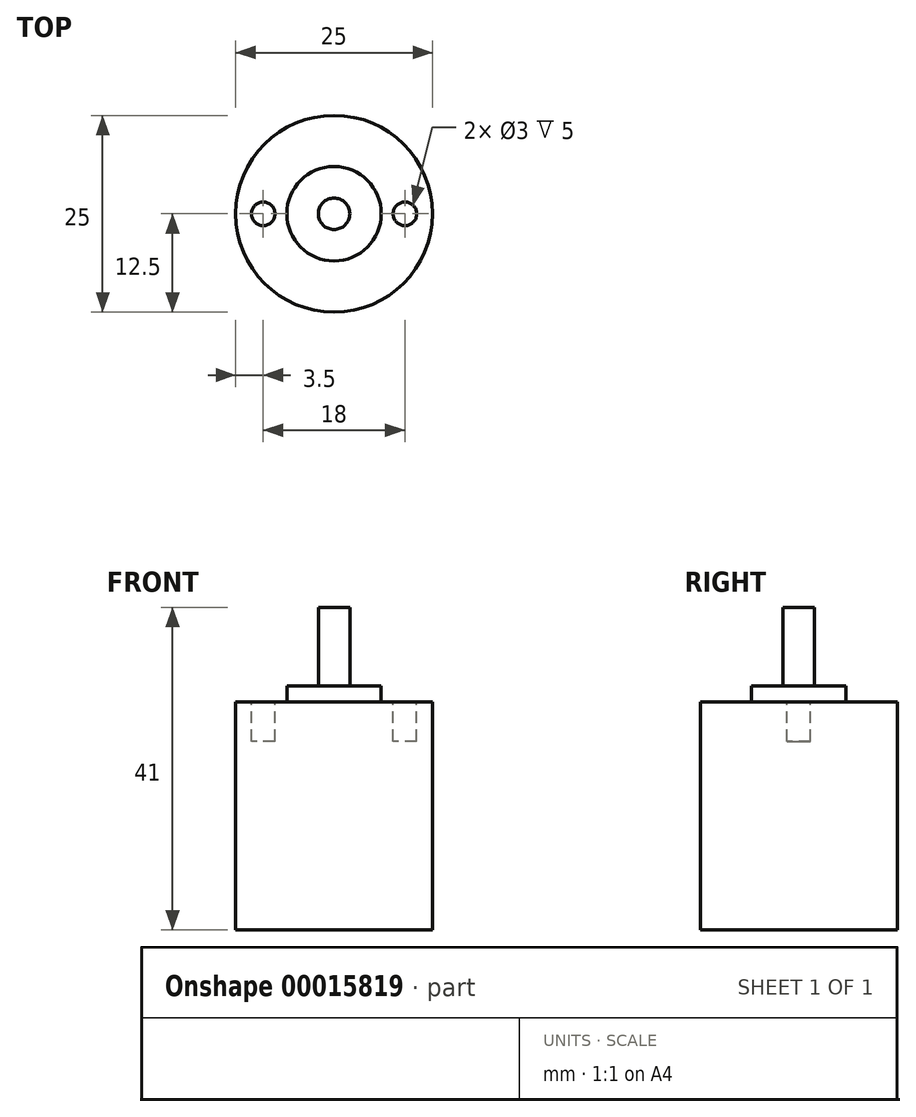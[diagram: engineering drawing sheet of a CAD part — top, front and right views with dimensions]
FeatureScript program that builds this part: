
annotation { "Feature Type Name" : "Feature", "Feature Type Description" : "" }
export const myFeature = defineFeature(function(context is Context, id is Id, definition is map)
    precondition{}
    {
        {
            var Q0;
            Q0=qCreatedBy(makeId("Top.planeOp"),FACE);
            var sketch = newSketch(context, id + "F0", { "sketchPlane" : qUnion([Q0])});
            skCircle(sketch, "E0", {"center": v(0, 0) * mm, "radius": 12.5 * mm});
            skSolve(sketch);
        }
        {
            var Q0;
            Q0=qSketchRegion(id+"F0",true);
            extrude(context, id + "F1", {"entities" : qUnion([Q0]), "depth" : 29 * mm});
        }
        {
            var Q0;
            Q0=makeQuery(id+"F1.opExtrude","CAP_FACE",FACE,{"disambiguationData":[OSD([sQuery(id+"F0.wireOp",EDGE,"E0")])],"isStart":false});
            var sketch = newSketch(context, id + "F2", { "sketchPlane" : qUnion([Q0])});
            skCircle(sketch, "E1", {"center": v(0, 0) * mm, "radius": 6 * mm});
            skSolve(sketch);
        }
        {
            var Q0;
            Q0 = qSketchRegion(id + "F2", true);
            extrude(context, id + "F3", {"entities" : qUnion([Q0]), "operationType" : NewBodyOperationType.ADD, "depth" : 2 * mm});
        }
        {
            var Q0;
            Q0=makeQuery(id+"F3.opExtrude","CAP_FACE",FACE,{"disambiguationData":[OSD([sQuery(id+"F2.wireOp",EDGE,"E1")])],"isStart":false});
            var sketch = newSketch(context, id + "F4", { "sketchPlane" : qUnion([Q0])});
            skCircle(sketch, "E2", {"center": v(0, 0) * mm, "radius": 2 * mm});
            skSolve(sketch);
        }
        {
            var Q0;
            Q0 = qSketchRegion(id + "F4", true);
            extrude(context, id + "F5", {"entities" : qUnion([Q0]), "operationType" : NewBodyOperationType.ADD, "depth" : 10 * mm});
        }
        {
            var Q0;
            Q0=makeQuery(id+"F1.opExtrude","CAP_FACE",FACE,{"disambiguationData":[OSD([sQuery(id+"F0.wireOp",EDGE,"E0")])],"isStart":false});
            var sketch = newSketch(context, id + "F6", { "sketchPlane" : qUnion([Q0])});
            skLineSegment(sketch, "E3", {"start": v(-9, 0) * mm, "end": v(9, 0) * mm, "construction": true});
            skPoint(sketch, "E4", {"position": v(0, 0) * mm});
            skCircle(sketch, "E5", {"center": v(-9, 0) * mm, "radius": 1.5 * mm});
            skCircle(sketch, "E6", {"center": v(9, 0) * mm, "radius": 1.5 * mm});
            skSolve(sketch);
        }
        {
            var Q0;
            Q0 = qSketchRegion(id + "F6", true);
            extrude(context, id + "F7", {"entities" : qUnion([Q0]), "operationType" : NewBodyOperationType.REMOVE, "oppositeDirection" : true, "depth" : 5 * mm});
        }
    });
